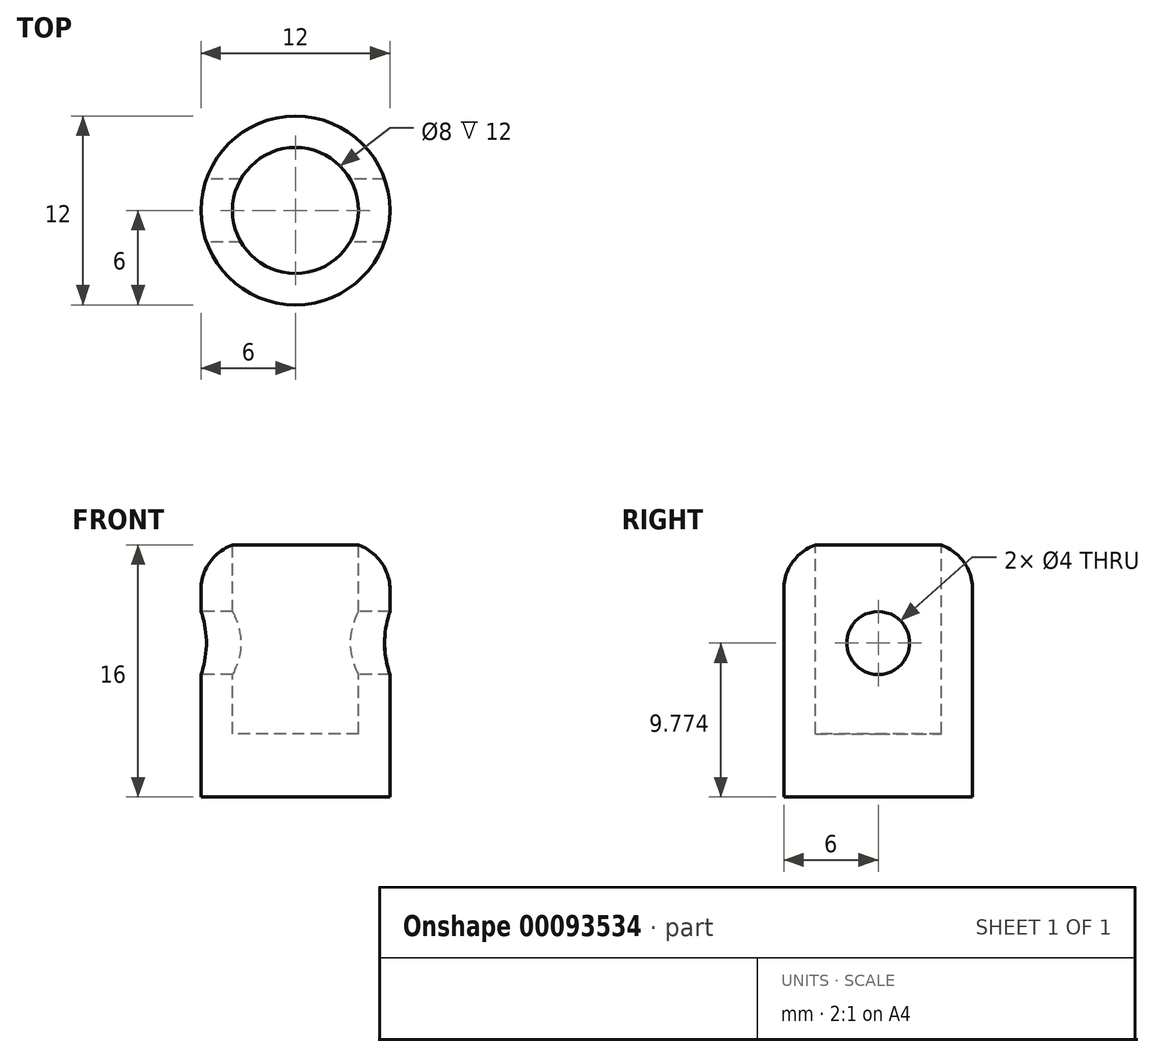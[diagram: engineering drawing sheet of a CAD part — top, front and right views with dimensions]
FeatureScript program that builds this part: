
annotation { "Feature Type Name" : "Feature", "Feature Type Description" : "" }
export const myFeature = defineFeature(function(context is Context, id is Id, definition is map)
    precondition{}
    {
        {
            var Q0;
            Q0=qCreatedBy(makeId("Top.planeOp"),FACE);
            var sketch = newSketch(context, id + "F0", { "sketchPlane" : qUnion([Q0])});
            skCircle(sketch, "E0", {"center": v(0, 0) * mm, "radius": 6 * mm});
            skSolve(sketch);
        }
        {
            var Q0;
            Q0 = qSketchRegion(id + "F0", true);
            extrude(context, id + "F1", {"entities" : qUnion([Q0]), "depth" : 16 * mm});
        }
        {
            var Q0;
            Q0=qCreatedBy(makeId("Right.planeOp"),FACE);
            var sketch = newSketch(context, id + "F2", { "sketchPlane" : qUnion([Q0])});
            skCircle(sketch, "E1", {"center": v(0, 9.77) * mm, "radius": 2 * mm});
            skSolve(sketch);
        }
        {
            var Q0;
            Q0 = qSketchRegion(id + "F2", true);
            extrude(context, id + "F3", {"entities" : qUnion([Q0]), "operationType" : NewBodyOperationType.REMOVE, "depth" : 25 * mm, "symmetric" : true});
        }
        {
            var Q0;
            Q0=makeQuery(id+"F1.opExtrude","CAP_FACE",FACE,{"disambiguationData":[OSD([sQuery(id+"F0.wireOp",EDGE,"E0")])],"isStart":false});
            var sketch = newSketch(context, id + "F4", { "sketchPlane" : qUnion([Q0])});
            skCircle(sketch, "E2", {"center": v(0, 0) * mm, "radius": 4 * mm});
            skSolve(sketch);
        }
        {
            var Q0;
            Q0 = qSketchRegion(id + "F4", true);
            extrude(context, id + "F5", {"entities" : qUnion([Q0]), "operationType" : NewBodyOperationType.REMOVE, "oppositeDirection" : true, "depth" : 12 * mm});
        }
        {
            var Q0;
            Q0=makeQuery(id+"F1.opExtrude","CAP_EDGE",EDGE,{"disambiguationData":[OSD([sQuery(id+"F0.wireOp",EDGE,"E0")])],"isStart":false});
            fillet(context, id + "F6", {"entities" : qUnion([Q0]), "radius" : 3 * mm, "tangentPropagation" : true, "allowEdgeOverflow" : false});
        }
    });
